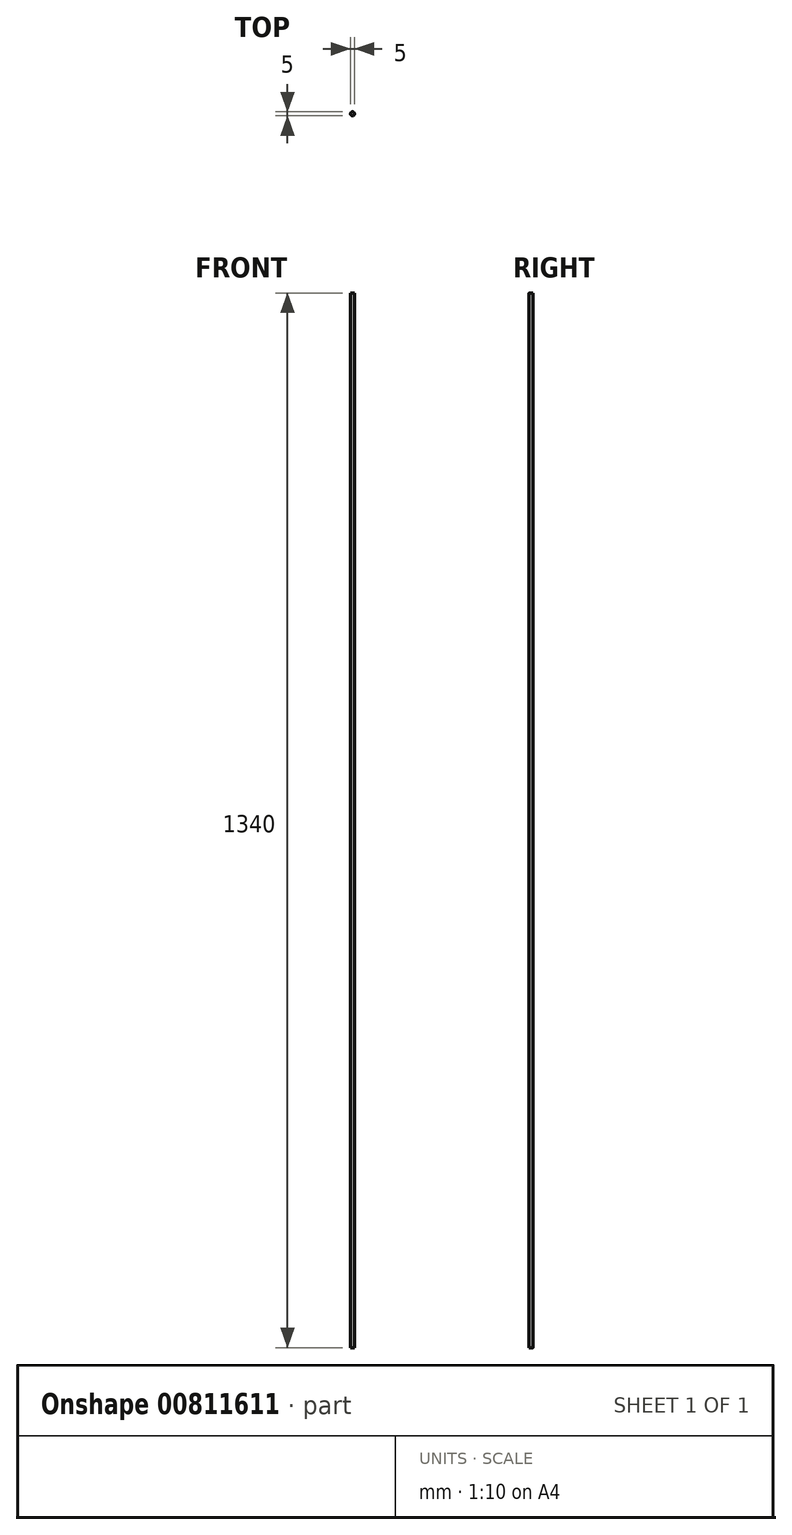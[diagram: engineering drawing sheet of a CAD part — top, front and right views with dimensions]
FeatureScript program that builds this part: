
annotation { "Feature Type Name" : "Feature", "Feature Type Description" : "" }
export const myFeature = defineFeature(function(context is Context, id is Id, definition is map)
    precondition{}
    {
        {
            var Q0;
            Q0=qCreatedBy(makeId("Top.planeOp"),FACE);
            var sketch = newSketch(context, id + "F0", { "sketchPlane" : qUnion([Q0])});
            skCircle(sketch, "E0", {"center": v(0, 0) * mm, "radius": 2.5 * mm});
            skSolve(sketch);
        }
        {
            var Q0;
            Q0=qSketchRegion(id+"F0",true);
            extrude(context, id + "F1", {"entities" : qUnion([Q0]), "depth" : 1340 * mm, "offsetDistance" : 25 * mm});
        }
    });
